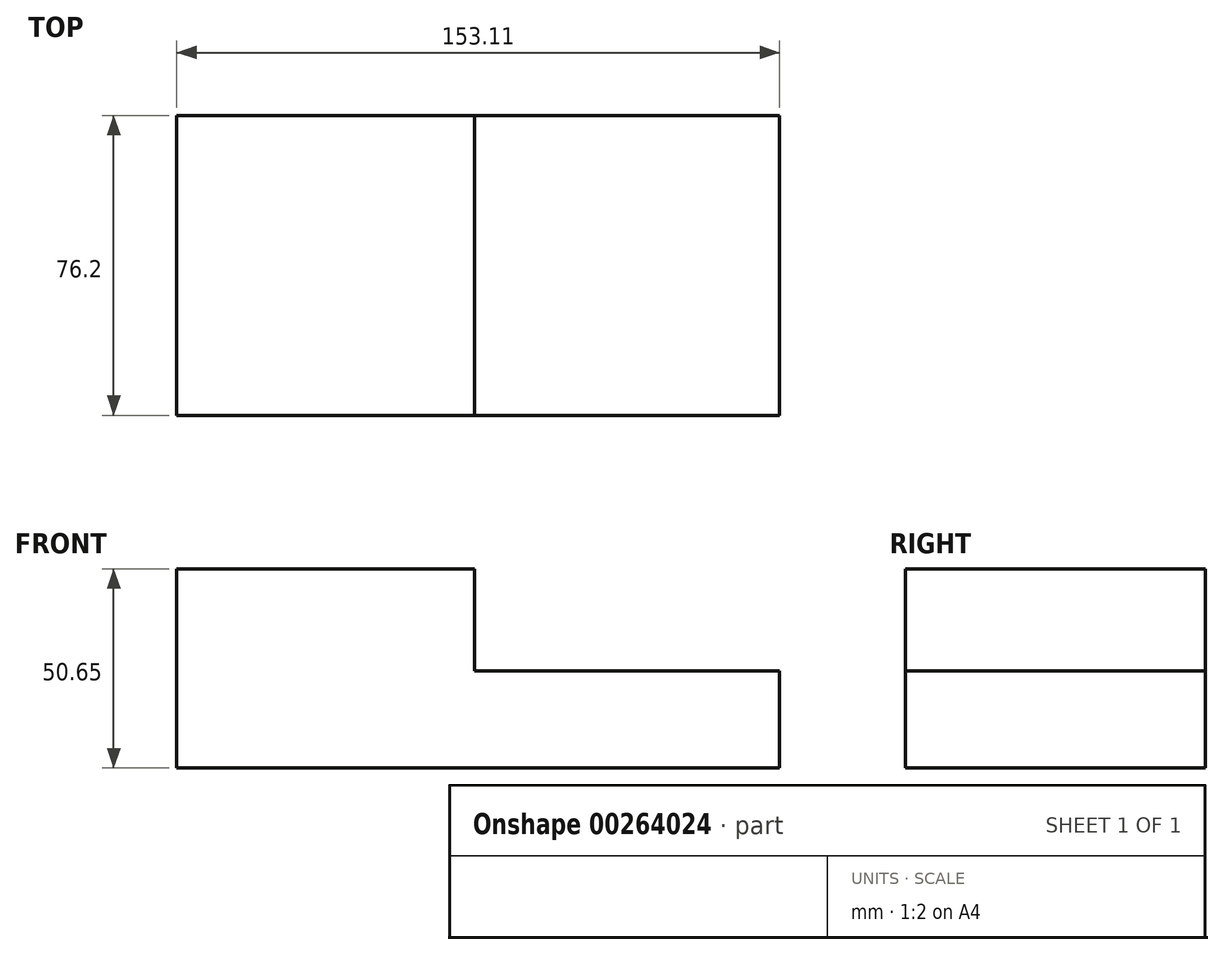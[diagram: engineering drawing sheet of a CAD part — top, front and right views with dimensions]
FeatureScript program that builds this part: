
annotation { "Feature Type Name" : "Feature", "Feature Type Description" : "" }
export const myFeature = defineFeature(function(context is Context, id is Id, definition is map)
    precondition{}
    {
        {
            var Q0;
            Q0=qCreatedBy(makeId("Front.planeOp"),FACE);
            var sketch = newSketch(context, id + "F0", { "sketchPlane" : qUnion([Q0])});
            skLineSegment(sketch, "E0.bottom", {"start": v(0, 0) * mm, "end": v(76.27, 0) * mm});
            skLineSegment(sketch, "E0.top", {"start": v(0, 25.61) * mm, "end": v(76.27, 25.61) * mm});
            skLineSegment(sketch, "E0.left", {"start": v(0, 0) * mm, "end": v(0, 25.61) * mm});
            skLineSegment(sketch, "E0.right", {"start": v(76.27, 0) * mm, "end": v(76.27, 25.61) * mm});
            skSolve(sketch);
        }
        {
            var Q0;
            Q0=makeQuery(id+"F0.imprint","IMPRINT",FACE,{"disambiguationData":[TD([[makeQuery(id+"F0.imprint","IMPRINT",EDGE,{"derivedFrom":sQuery(id+"F0.wireOp",EDGE,"E0.bottom")}),1.0]])]});
            extrude(context, id + "F1", {"entities" : qUnion([Q0]), "depth" : 76.2 * mm});
        }
        {
            var Q0;
            Q0=makeQuery(id+"F1.opExtrude","SWEPT_BODY",BODY,{"disambiguationData":[OSD([sQuery(id+"F0.wireOp",EDGE,"E0.bottom"),sQuery(id+"F0.wireOp",EDGE,"E0.top"),sQuery(id+"F0.wireOp",EDGE,"E0.left"),sQuery(id+"F0.wireOp",EDGE,"E0.right")])]});
            deleteBodies(context, id + "F2", {"entities" : qUnion([Q0])});
        }
        {
            var Q0;
            Q0=qCreatedBy(makeId("Front.planeOp"),FACE);
            var sketch = newSketch(context, id + "F3", { "sketchPlane" : qUnion([Q0])});
            skLineSegment(sketch, "E1.bottom", {"start": v(-75.7, 0) * mm, "end": v(77.42, 0) * mm});
            skLineSegment(sketch, "E1.top", {"start": v(-75.7, 50.65) * mm, "end": v(77.42, 50.65) * mm});
            skLineSegment(sketch, "E1.left", {"start": v(-75.7, 0) * mm, "end": v(-75.7, 50.65) * mm});
            skLineSegment(sketch, "E1.right", {"start": v(77.42, 0) * mm, "end": v(77.42, 50.65) * mm});
            skSolve(sketch);
        }
        {
            var Q0;
            Q0=makeQuery(id+"F3.imprint","IMPRINT",FACE,{"disambiguationData":[TD([[makeQuery(id+"F3.imprint","IMPRINT",EDGE,{"derivedFrom":sQuery(id+"F3.wireOp",EDGE,"E1.bottom")}),1.0]])]});
            extrude(context, id + "F4", {"entities" : qUnion([Q0]), "oppositeDirection" : true, "depth" : 76.2 * mm});
        }
        {
            var Q0;
            Q0=makeQuery(id+"F4.opExtrude","CAP_FACE",FACE,{"disambiguationData":[OSD([sQuery(id+"F3.wireOp",EDGE,"E1.bottom"),sQuery(id+"F3.wireOp",EDGE,"E1.top"),sQuery(id+"F3.wireOp",EDGE,"E1.left"),sQuery(id+"F3.wireOp",EDGE,"E1.right")])],"isStart":true});
            var sketch = newSketch(context, id + "F5", { "sketchPlane" : qUnion([Q0])});
            skLineSegment(sketch, "E2.bottom", {"start": v(0, 24.75) * mm, "end": v(77.42, 24.75) * mm});
            skLineSegment(sketch, "E2.top", {"start": v(0, 50.65) * mm, "end": v(77.42, 50.65) * mm});
            skLineSegment(sketch, "E2.left", {"start": v(0, 24.75) * mm, "end": v(0, 50.65) * mm});
            skLineSegment(sketch, "E2.right", {"start": v(77.42, 24.75) * mm, "end": v(77.42, 50.65) * mm});
            skSolve(sketch);
        }
        {
            var Q0;
            Q0 = qSketchRegion(id + "F5", true);
            extrude(context, id + "F6", {"entities" : qUnion([Q0]), "operationType" : NewBodyOperationType.REMOVE, "endBound" : BoundingType.UP_TO_NEXT, "oppositeDirection" : true, "depth" : 25.4 * mm});
        }
    });
